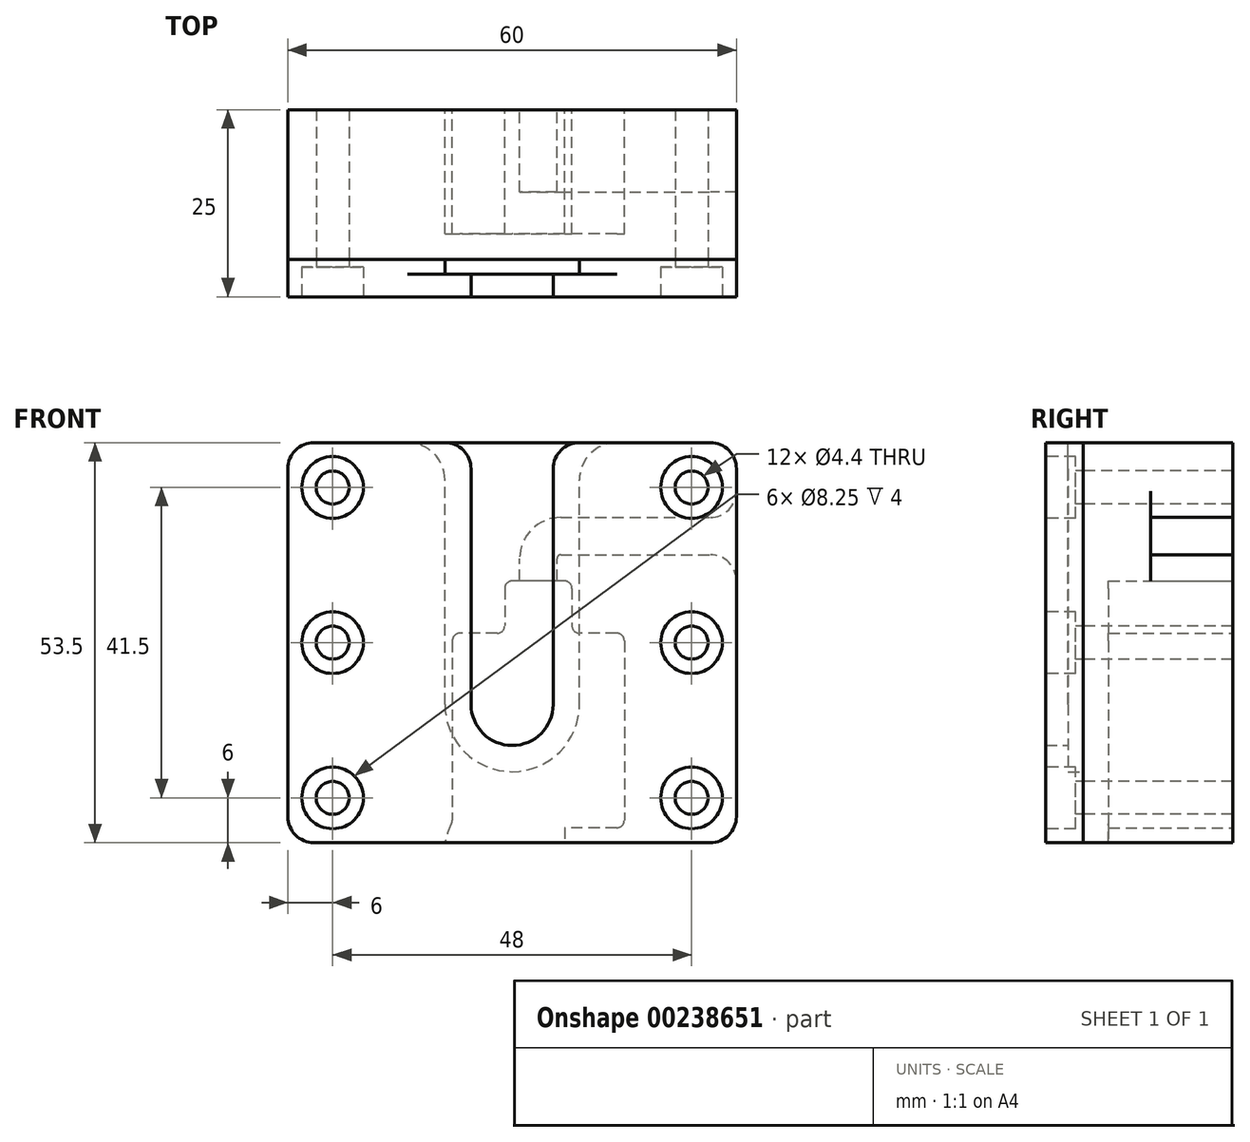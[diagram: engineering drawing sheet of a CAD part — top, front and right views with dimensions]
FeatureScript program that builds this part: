
annotation { "Feature Type Name" : "Feature", "Feature Type Description" : "" }
export const myFeature = defineFeature(function(context is Context, id is Id, definition is map)
    precondition{}
    {
        {
            var Q0;
            Q0=qCreatedBy(makeId("Front.planeOp"),FACE);
            var sketch = newSketch(context, id + "F0", { "sketchPlane" : qUnion([Q0])});
            skLineSegment(sketch, "E0.bottom", {"start": v(-26.5, 0) * mm, "end": v(26.5, 0) * mm});
            skLineSegment(sketch, "E0.top", {"start": v(-26.5, -53.5) * mm, "end": v(26.5, -53.5) * mm});
            skLineSegment(sketch, "E0.left", {"start": v(-30, -3.5) * mm, "end": v(-30, -50) * mm});
            skLineSegment(sketch, "E0.right", {"start": v(30, -3.5) * mm, "end": v(30, -50) * mm});
            skArc(sketch, "E1", {"start": v(-9, -35) * mm, "mid": v(0, -44) * mm, "end": v(9, -35) * mm});
            skLineSegment(sketch, "E2", {"start": v(-9, -35) * mm, "end": v(-9, 0) * mm});
            skLineSegment(sketch, "E3.MirrorCS", {"start": v(9, -35) * mm, "end": v(9, 0) * mm});
            skArc(sketch, "E4", {"start": v(-5.5, -35) * mm, "mid": v(0, -40.5) * mm, "end": v(5.5, -35) * mm});
            skArc(sketch, "E5", {"start": v(-5.5, -3.5) * mm, "mid": v(-6.53, -1.03) * mm, "end": v(-9, 0) * mm});
            skLineSegment(sketch, "E6", {"start": v(-5.5, -3.5) * mm, "end": v(-5.5, -35) * mm});
            skLineSegment(sketch, "E7.MirrorCS", {"start": v(5.5, -3.5) * mm, "end": v(5.5, -35) * mm});
            skArc(sketch, "E8.MirrorCS", {"start": v(5.5, -3.5) * mm, "mid": v(6.53, -1.03) * mm, "end": v(9, 0) * mm});
            skPoint(sketch, "E9.visualSharp", {"position": v(-30, 0) * mm});
            skArc(sketch, "E9.filletArc", {"start": v(-26.5, 0) * mm, "mid": v(-28.97, -1.03) * mm, "end": v(-30, -3.5) * mm});
            skPoint(sketch, "E10.visualSharp", {"position": v(30, 0) * mm});
            skArc(sketch, "E10.filletArc", {"start": v(30, -3.5) * mm, "mid": v(28.97, -1.03) * mm, "end": v(26.5, 0) * mm});
            skPoint(sketch, "E11.visualSharp", {"position": v(30, -53.5) * mm});
            skArc(sketch, "E11.filletArc", {"start": v(26.5, -53.5) * mm, "mid": v(28.97, -52.47) * mm, "end": v(30, -50) * mm});
            skPoint(sketch, "E12.visualSharp", {"position": v(-30, -53.5) * mm});
            skArc(sketch, "E12.filletArc", {"start": v(-30, -50) * mm, "mid": v(-28.97, -52.47) * mm, "end": v(-26.5, -53.5) * mm});
            skSolve(sketch);
        }
        {
            var Q0;
            Q0=makeQuery(id+"F0.imprint","IMPRINT",FACE,{"disambiguationData":[TD([[makeQuery(id+"F0.imprint","IMPRINT",EDGE,{"derivedFrom":sQuery(id+"F0.wireOp",EDGE,"E0.top")}),1.0]])]});
            var Q1;
            Q1=makeQuery(id+"F0.imprint","IMPRINT",FACE,{"disambiguationData":[TD([[makeQuery(id+"F0.imprint","IMPRINT",EDGE,{"derivedFrom":sQuery(id+"F0.wireOp",EDGE,"E1")}),1.0]])]});
            extrude(context, id + "F1", {"entities" : qUnion([Q0, Q1]), "depth" : 5 * mm});
        }
        {
            var Q0;
            Q0=makeQuery(id+"F0.imprint","IMPRINT",FACE,{"disambiguationData":[TD([[makeQuery(id+"F0.imprint","IMPRINT",EDGE,{"derivedFrom":sQuery(id+"F0.wireOp",EDGE,"E1")}),1.0]])]});
            extrude(context, id + "F2", {"entities" : qUnion([Q0]), "operationType" : NewBodyOperationType.REMOVE, "depth" : 2 * mm});
        }
        {
            var Q0;
            Q0 = qSketchRegion(id + "F0", true);
            extrude(context, id + "F3", {"entities" : qUnion([Q0]), "oppositeDirection" : true, "depth" : 20 * mm});
        }
        {
            var Q0;
            Q0=makeQuery(id+"F3.opExtrude","CAP_FACE",FACE,{"disambiguationData":[OSD([sQuery(id+"F0.wireOp",EDGE,"E0.bottom"),sQuery(id+"F0.wireOp",EDGE,"E0.top"),sQuery(id+"F0.wireOp",EDGE,"E0.left"),sQuery(id+"F0.wireOp",EDGE,"E0.right"),sQuery(id+"F0.wireOp",EDGE,"E9.filletArc"),sQuery(id+"F0.wireOp",EDGE,"E10.filletArc"),sQuery(id+"F0.wireOp",EDGE,"E11.filletArc"),sQuery(id+"F0.wireOp",EDGE,"E12.filletArc")])],"isStart":false});
            var sketch = newSketch(context, id + "F4", { "sketchPlane" : qUnion([Q0])});
            skLineSegment(sketch, "E13.bottom", {"start": v(-15, -25.5) * mm, "end": v(-8, -25.5) * mm});
            skLineSegment(sketch, "E13.top", {"start": v(-15, -51.5) * mm, "end": v(-7, -51.5) * mm});
            skLineSegment(sketch, "E13.left", {"start": v(-15, -25.5) * mm, "end": v(-15, -51.5) * mm});
            skLineSegment(sketch, "E13.right", {"start": v(8, -25.5) * mm, "end": v(8, -51.5) * mm});
            skLineSegment(sketch, "E14.bottom", {"start": v(8, -51.5) * mm, "end": v(9, -51.5) * mm});
            skLineSegment(sketch, "E14.top", {"start": v(-7, -53.5) * mm, "end": v(9, -53.5) * mm});
            skLineSegment(sketch, "E14.left", {"start": v(-7, -51.5) * mm, "end": v(-7, -53.5) * mm});
            skLineSegment(sketch, "E14.right", {"start": v(9, -51.5) * mm, "end": v(9, -53.5) * mm});
            skLineSegment(sketch, "E15.bottom", {"start": v(-8, -18.5) * mm, "end": v(1, -18.5) * mm});
            skLineSegment(sketch, "E15.left", {"start": v(-8, -18.5) * mm, "end": v(-8, -25.5) * mm});
            skLineSegment(sketch, "E15.right", {"start": v(1, -18.5) * mm, "end": v(1, -25.5) * mm});
            skLineSegment(sketch, "E16", {"start": v(-3.5, -27.68) * mm, "end": v(-3.5, -18.5) * mm, "construction": true});
            skLineSegment(sketch, "E17", {"start": v(-6, -18.5) * mm, "end": v(-6, -15.5) * mm});
            skLineSegment(sketch, "E18.MirrorCS", {"start": v(-1, -18.5) * mm, "end": v(-1, -15.5) * mm});
            skArc(sketch, "E19", {"start": v(-6, -15.5) * mm, "mid": v(-6.15, -15.15) * mm, "end": v(-6.5, -15) * mm});
            skArc(sketch, "E20", {"start": v(-1, -15.5) * mm, "mid": v(-2.61, -11.61) * mm, "end": v(-6.5, -10) * mm});
            skLineSegment(sketch, "E21", {"start": v(-6.5, -15) * mm, "end": v(-26.5, -15) * mm});
            skLineSegment(sketch, "E22", {"start": v(-6.5, -10) * mm, "end": v(-26.5, -10) * mm});
            skLineSegment(sketch, "E23.0", {"start": v(-30, -3.5) * mm, "end": v(-30, -50) * mm});
            skArc(sketch, "E24.0", {"start": v(-30, -3.5) * mm, "mid": v(-28.97, -1.03) * mm, "end": v(-26.5, 0) * mm});
            skLineSegment(sketch, "E24.1", {"start": v(26.5, 0) * mm, "end": v(-26.5, 0) * mm});
            skArc(sketch, "E24.2", {"start": v(26.5, 0) * mm, "mid": v(28.97, -1.03) * mm, "end": v(30, -3.5) * mm});
            skLineSegment(sketch, "E24.3", {"start": v(30, -3.5) * mm, "end": v(30, -50) * mm});
            skArc(sketch, "E24.4", {"start": v(30, -50) * mm, "mid": v(28.97, -52.47) * mm, "end": v(26.5, -53.5) * mm});
            skLineSegment(sketch, "E24.5", {"start": v(26.5, -53.5) * mm, "end": v(-26.5, -53.5) * mm});
            skArc(sketch, "E24.6", {"start": v(-26.5, -53.5) * mm, "mid": v(-28.97, -52.47) * mm, "end": v(-30, -50) * mm});
            skArc(sketch, "E25", {"start": v(-30, -6.5) * mm, "mid": v(-28.97, -8.97) * mm, "end": v(-26.5, -10) * mm});
            skArc(sketch, "E26", {"start": v(-26.5, -15) * mm, "mid": v(-28.97, -16.03) * mm, "end": v(-30, -18.5) * mm});
            skLineSegment(sketch, "E27.trimOffspring", {"start": v(1, -25.5) * mm, "end": v(8, -25.5) * mm});
            skSolve(sketch);
        }
        {
            var Q0;
            Q0=makeQuery(id+"F4.imprint","IMPRINT",FACE,{"disambiguationData":[TD([[makeQuery(id+"F4.imprint","IMPRINT",EDGE,{"derivedFrom":sQuery(id+"F4.wireOp",EDGE,"E13.bottom")}),-1.0]])]});
            extrude(context, id + "F5", {"entities" : qUnion([Q0]), "operationType" : NewBodyOperationType.REMOVE, "oppositeDirection" : true, "depth" : 16.6 * mm});
        }
        {
            var Q0;
            {var subQ1=sQuery(id+"F4.wireOp",EDGE,"E17");Q0=makeQuery(id+"F4.imprint","IMPRINT",FACE,{"disambiguationData":[TD([[makeQuery(id+"F4.imprint","IMPRINT",EDGE,{"derivedFrom":subQ1}),-1.0]])]});}
            extrude(context, id + "F6", {"entities" : qUnion([Q0]), "operationType" : NewBodyOperationType.REMOVE, "oppositeDirection" : true, "depth" : 11 * mm});
        }
        {
            var Q0;
            Q0=makeQuery(id+"F6.boolean.opBoolean","COPY",EDGE,{"derivedFrom":makeQuery(id+"F6.opExtrude","SWEPT_EDGE",EDGE,{"disambiguationData":[OSD([sQuery(id+"F4.wireOp",EDGE,"E15.bottom"),sQuery(id+"F4.wireOp",EDGE,"E18.MirrorCS")])]})});
            var Q1;
            Q1=makeQuery(id+"F5goFadYqqWBrVZ_2.opFillet","BLEND_EDGE",EDGE,{"blendedFrom":[makeQuery(id+"F6.boolean.opBoolean","COPY",EDGE,{"derivedFrom":makeQuery(id+"F6.opExtrude","CAP_EDGE",EDGE,{"disambiguationData":[OSD([sQuery(id+"F4.wireOp",EDGE,"E17")])],"isStart":false})}),makeQuery(id+"F5.boolean.opBoolean","COPY",FACE,{"derivedFrom":makeQuery(id+"F5.opExtrude","SWEPT_FACE",FACE,{"disambiguationData":[OSD([sQuery(id+"F4.wireOp",EDGE,"E15.bottom")])]})})],"blendedInto":[makeQuery(id+"F5.boolean.opBoolean","COPY",FACE,{"derivedFrom":makeQuery(id+"F5.opExtrude","SWEPT_FACE",FACE,{"disambiguationData":[OSD([sQuery(id+"F4.wireOp",EDGE,"E15.bottom")])]})})]});
            var Q2;
            Q2=makeQuery(id+"F6.boolean.opBoolean","COPY",EDGE,{"derivedFrom":makeQuery(id+"F6.opExtrude","SWEPT_EDGE",EDGE,{"disambiguationData":[OSD([sQuery(id+"F4.wireOp",EDGE,"E15.bottom"),sQuery(id+"F4.wireOp",EDGE,"E17")])]})});
            var Q3;
            Q3=makeQuery(id+"F5.boolean.opBoolean","COPY",EDGE,{"derivedFrom":makeQuery(id+"F5.opExtrude","SWEPT_EDGE",EDGE,{"disambiguationData":[OSD([sQuery(id+"F4.wireOp",EDGE,"E15.bottom"),sQuery(id+"F4.wireOp",EDGE,"E15.right")])]})});
            var Q4;
            Q4=makeQuery(id+"F5.boolean.opBoolean","COPY",EDGE,{"derivedFrom":makeQuery(id+"F5.opExtrude","SWEPT_EDGE",EDGE,{"disambiguationData":[OSD([sQuery(id+"F4.wireOp",EDGE,"E15.bottom"),sQuery(id+"F4.wireOp",EDGE,"E15.left")])]})});
            var Q5;
            Q5=makeQuery(id+"F5.boolean.opBoolean","COPY",EDGE,{"derivedFrom":makeQuery(id+"F5.opExtrude","SWEPT_EDGE",EDGE,{"disambiguationData":[OSD([sQuery(id+"F4.wireOp",EDGE,"E13.bottom"),sQuery(id+"F4.wireOp",EDGE,"E15.left")])]})});
            var Q6;
            Q6=makeQuery(id+"F5.boolean.opBoolean","COPY",EDGE,{"derivedFrom":makeQuery(id+"F5.opExtrude","SWEPT_EDGE",EDGE,{"disambiguationData":[OSD([sQuery(id+"F4.wireOp",EDGE,"E15.right"),sQuery(id+"F4.wireOp",EDGE,"E27.trimOffspring")])]})});
            var Q7;
            Q7=makeQuery(id+"F5.boolean.opBoolean","COPY",EDGE,{"derivedFrom":makeQuery(id+"F5.opExtrude","SWEPT_EDGE",EDGE,{"disambiguationData":[OSD([sQuery(id+"F4.wireOp",EDGE,"E13.bottom"),sQuery(id+"F4.wireOp",EDGE,"E13.left")])]})});
            var Q8;
            Q8=makeQuery(id+"F5.boolean.opBoolean","COPY",EDGE,{"derivedFrom":makeQuery(id+"F5.opExtrude","SWEPT_EDGE",EDGE,{"disambiguationData":[OSD([sQuery(id+"F4.wireOp",EDGE,"E13.right"),sQuery(id+"F4.wireOp",EDGE,"E14.bottom")])]})});
            var Q9;
            Q9=makeQuery(id+"F5.boolean.opBoolean","COPY",EDGE,{"derivedFrom":makeQuery(id+"F5.opExtrude","SWEPT_EDGE",EDGE,{"disambiguationData":[OSD([sQuery(id+"F4.wireOp",EDGE,"E14.left"),sQuery(id+"F4.wireOp",EDGE,"E24.5")])]})});
            var Q10;
            Q10=makeQuery(id+"F5.boolean.opBoolean","COPY",EDGE,{"derivedFrom":makeQuery(id+"F5.opExtrude","SWEPT_EDGE",EDGE,{"disambiguationData":[OSD([sQuery(id+"F4.wireOp",EDGE,"E14.right"),sQuery(id+"F4.wireOp",EDGE,"E24.5")])]})});
            var Q11;
            Q11=makeQuery(id+"F5.boolean.opBoolean","COPY",EDGE,{"derivedFrom":makeQuery(id+"F5.opExtrude","SWEPT_EDGE",EDGE,{"disambiguationData":[OSD([sQuery(id+"F4.wireOp",EDGE,"E13.right"),sQuery(id+"F4.wireOp",EDGE,"E27.trimOffspring")])]})});
            var Q12;
            Q12=makeQuery(id+"F5.boolean.opBoolean","COPY",EDGE,{"derivedFrom":makeQuery(id+"F5.opExtrude","SWEPT_EDGE",EDGE,{"disambiguationData":[OSD([sQuery(id+"F4.wireOp",EDGE,"E13.top"),sQuery(id+"F4.wireOp",EDGE,"E13.left")])]})});
            fillet(context, id + "F7", {"entities" : qUnion([Q0, Q1, Q2, Q3, Q4, Q5, Q6, Q7, Q8, Q9, Q10, Q11, Q12]), "radius" : 1 * mm, "tangentPropagation" : true, "allowEdgeOverflow" : false});
        }
        {
            var Q0;
            Q0=makeQuery(id+"F7.opFillet","BLEND_EDGE",EDGE,{"blendedFrom":[makeQuery(id+"F5.boolean.opBoolean","COPY",EDGE,{"derivedFrom":makeQuery(id+"F5.opExtrude","SWEPT_EDGE",EDGE,{"disambiguationData":[OSD([sQuery(id+"F4.wireOp",EDGE,"E13.right"),sQuery(id+"F4.wireOp",EDGE,"E14.bottom")])]})}),makeQuery(id+"F5.boolean.opBoolean","COPY",FACE,{"derivedFrom":makeQuery(id+"F5.opExtrude","SWEPT_FACE",FACE,{"disambiguationData":[OSD([sQuery(id+"F4.wireOp",EDGE,"E14.right")])]})})],"blendedInto":[makeQuery(id+"F5.boolean.opBoolean","COPY",FACE,{"derivedFrom":makeQuery(id+"F5.opExtrude","SWEPT_FACE",FACE,{"disambiguationData":[OSD([sQuery(id+"F4.wireOp",EDGE,"E14.right")])]})})]});
            fillet(context, id + "F8", {"entities" : qUnion([Q0]), "radius" : 10 * mm, "tangentPropagation" : true, "allowEdgeOverflow" : false});
        }
        {
            var Q0;
            Q0=makeQuery(id+"F1.opExtrude","CAP_FACE",FACE,{"disambiguationData":[OSD([sQuery(id+"F0.wireOp",EDGE,"E0.bottom"),sQuery(id+"F0.wireOp",EDGE,"E0.top"),sQuery(id+"F0.wireOp",EDGE,"E0.left"),sQuery(id+"F0.wireOp",EDGE,"E0.right"),sQuery(id+"F0.wireOp",EDGE,"E4"),sQuery(id+"F0.wireOp",EDGE,"E5"),sQuery(id+"F0.wireOp",EDGE,"E6"),sQuery(id+"F0.wireOp",EDGE,"E7.MirrorCS"),sQuery(id+"F0.wireOp",EDGE,"E8.MirrorCS"),sQuery(id+"F0.wireOp",EDGE,"E9.filletArc"),sQuery(id+"F0.wireOp",EDGE,"E10.filletArc"),sQuery(id+"F0.wireOp",EDGE,"E11.filletArc"),sQuery(id+"F0.wireOp",EDGE,"E12.filletArc")])],"isStart":false});
            var sketch = newSketch(context, id + "F9", { "sketchPlane" : qUnion([Q0])});
            skLineSegment(sketch, "E28.bottom", {"start": v(-24, -6) * mm, "end": v(24, -6) * mm, "construction": true});
            skLineSegment(sketch, "E28.top", {"start": v(-24, -47.5) * mm, "end": v(24, -47.5) * mm, "construction": true});
            skLineSegment(sketch, "E28.left", {"start": v(-24, -6) * mm, "end": v(-24, -47.5) * mm, "construction": true});
            skLineSegment(sketch, "E28.right", {"start": v(24, -6) * mm, "end": v(24, -47.5) * mm, "construction": true});
            skPoint(sketch, "E29", {"position": v(-24, -6) * mm});
            skPoint(sketch, "E30", {"position": v(24, -6) * mm});
            skPoint(sketch, "E31", {"position": v(24, -47.5) * mm});
            skPoint(sketch, "E32", {"position": v(-24, -47.5) * mm});
            skPoint(sketch, "E33", {"position": v(-24, -26.75) * mm});
            skPoint(sketch, "E34", {"position": v(24, -26.75) * mm});
            skSolve(sketch);
        }
        {
            var Q0;
            Q0=sQuery(id+"F9.wireOp",VERTEX,"E29");
            var Q1;
            Q1=sQuery(id+"F9.wireOp",VERTEX,"E30");
            var Q2;
            Q2=sQuery(id+"F9.wireOp",VERTEX,"E32");
            var Q3;
            Q3=sQuery(id+"F9.wireOp",VERTEX,"E31");
            var Q4;
            Q4=sQuery(id+"F9.wireOp",VERTEX,"E33");
            var Q5;
            Q5=sQuery(id+"F9.wireOp",VERTEX,"E34");
            var Q6;
            Q6=makeQuery(id+"F1.opExtrude","SWEPT_BODY",BODY,{"disambiguationData":[OSD([sQuery(id+"F0.wireOp",EDGE,"E0.bottom"),sQuery(id+"F0.wireOp",EDGE,"E0.top"),sQuery(id+"F0.wireOp",EDGE,"E0.left"),sQuery(id+"F0.wireOp",EDGE,"E0.right"),sQuery(id+"F0.wireOp",EDGE,"E4"),sQuery(id+"F0.wireOp",EDGE,"E5"),sQuery(id+"F0.wireOp",EDGE,"E6"),sQuery(id+"F0.wireOp",EDGE,"E7.MirrorCS"),sQuery(id+"F0.wireOp",EDGE,"E8.MirrorCS"),sQuery(id+"F0.wireOp",EDGE,"E9.filletArc"),sQuery(id+"F0.wireOp",EDGE,"E10.filletArc"),sQuery(id+"F0.wireOp",EDGE,"E11.filletArc"),sQuery(id+"F0.wireOp",EDGE,"E12.filletArc")])]});
            var Q7;
            Q7=makeQuery(id+"F3.opExtrude","SWEPT_BODY",BODY,{"disambiguationData":[OSD([sQuery(id+"F0.wireOp",EDGE,"E0.bottom"),sQuery(id+"F0.wireOp",EDGE,"E0.top"),sQuery(id+"F0.wireOp",EDGE,"E0.left"),sQuery(id+"F0.wireOp",EDGE,"E0.right"),sQuery(id+"F0.wireOp",EDGE,"E9.filletArc"),sQuery(id+"F0.wireOp",EDGE,"E10.filletArc"),sQuery(id+"F0.wireOp",EDGE,"E11.filletArc"),sQuery(id+"F0.wireOp",EDGE,"E12.filletArc")])]});
            hole(context, id + "F10", {"style" : HoleStyle.C_BORE, "endStyle" : HoleEndStyle.THROUGH, "standardTappedOrClearance" : lookupTablePath({ "standard" : "ISO", "fit" : "Normal", "size" : "M4", "type" : "Clearance" }), "standardBlindInLast" : lookupTablePath({ "fit" : "Standard", "standard" : "ISO", "size" : "M4", "type" : "Clearance" }), "holeDiameter" : 4.4 * mm, "cBoreDiameter" : 8.25 * mm, "cBoreDepth" : 4 * mm, "locations" : qUnion([Q0, Q1, Q2, Q3, Q4, Q5]), "scope" : qUnion([Q6, Q7]), "tappedDepth" : 12 * mm, "tapClearance" : 3});
        }
        {
            var Q0;
            Q0=makeQuery(id+"F5qNLjnjNo4RO4t_2.boolean.opBoolean","COPY",EDGE,{"derivedFrom":makeQuery(id+"F5qNLjnjNo4RO4t_2.opExtrude","TWEAK_EDGE",EDGE,{"derivedFrom":[makeQuery(id+"F2.boolean.opBoolean","COPY",FACE,{"derivedFrom":makeQuery(id+"F2.opExtrude","SWEPT_FACE",FACE,{"disambiguationData":[OSD([sQuery(id+"F0.wireOp",EDGE,"E3.MirrorCS")])]})}),makeQuery(id+"FWexJFam0BZQeY7_2.imprint","IMPRINT",EDGE,{"derivedFrom":sQuery(id+"FWexJFam0BZQeY7_2.wireOp",EDGE,"879efe7f-8b89-4b12-9335-ac03b7069748.0.3")})]})});
            var Q1;
            {var subQ0=sQuery(id+"F0.wireOp",EDGE,"E8.MirrorCS");var subQ1=sQuery(id+"F0.wireOp",EDGE,"E3.MirrorCS");var subQ2=sQuery(id+"F0.wireOp",EDGE,"E0.bottom");Q1=makeQuery(id+"F2.boolean.opBoolean","MERGE",EDGE,{"derivedFrom":[makeQuery(id+"F1.opExtrude","SWEPT_EDGE",EDGE,{"disambiguationData":[OSD([subQ2,subQ1,subQ0])]}),makeQuery(id+"F2.opExtrude","SWEPT_EDGE",EDGE,{"disambiguationData":[OSD([subQ2,subQ1,subQ0])]})]});}
            var Q2;
            Q2=makeQuery(id+"F5qNLjnjNo4RO4t_2.boolean.opBoolean","COPY",EDGE,{"derivedFrom":makeQuery(id+"F5qNLjnjNo4RO4t_2.opExtrude","TWEAK_EDGE",EDGE,{"derivedFrom":[makeQuery(id+"F2.boolean.opBoolean","COPY",FACE,{"derivedFrom":makeQuery(id+"F2.opExtrude","SWEPT_FACE",FACE,{"disambiguationData":[OSD([sQuery(id+"F0.wireOp",EDGE,"E2")])]})}),makeQuery(id+"FWexJFam0BZQeY7_2.imprint","IMPRINT",EDGE,{"derivedFrom":sQuery(id+"FWexJFam0BZQeY7_2.wireOp",EDGE,"879efe7f-8b89-4b12-9335-ac03b7069748.0.3")})]})});
            var Q3;
            {var subQ0=sQuery(id+"F0.wireOp",EDGE,"E5");var subQ1=sQuery(id+"F0.wireOp",EDGE,"E2");var subQ2=sQuery(id+"F0.wireOp",EDGE,"E0.bottom");Q3=makeQuery(id+"F2.boolean.opBoolean","MERGE",EDGE,{"derivedFrom":[makeQuery(id+"F1.opExtrude","SWEPT_EDGE",EDGE,{"disambiguationData":[OSD([subQ2,subQ1,subQ0])]}),makeQuery(id+"F2.opExtrude","SWEPT_EDGE",EDGE,{"disambiguationData":[OSD([subQ2,subQ1,subQ0])]})]});}
            fillet(context, id + "F11", {"entities" : qUnion([Q0, Q1, Q2, Q3]), "radius" : 5 * mm, "tangentPropagation" : true, "allowEdgeOverflow" : false});
        }
    });
